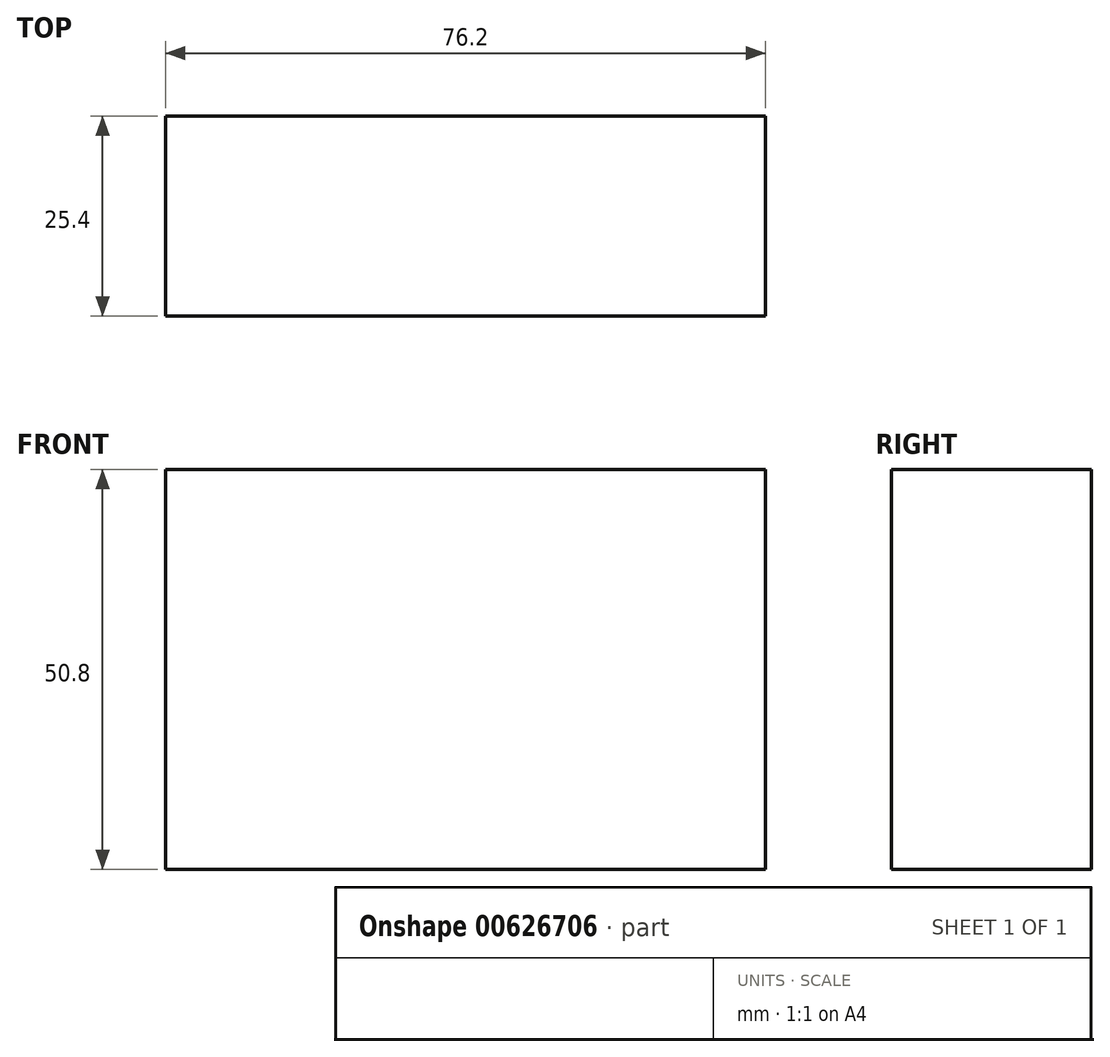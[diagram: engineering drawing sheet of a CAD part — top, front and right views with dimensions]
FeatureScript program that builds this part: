
annotation { "Feature Type Name" : "Feature", "Feature Type Description" : "" }
export const myFeature = defineFeature(function(context is Context, id is Id, definition is map)
    precondition{}
    {
        {
            var Q0;
            Q0=qCreatedBy(makeId("Front.planeOp"),FACE);
            var sketch = newSketch(context, id + "F0", { "sketchPlane" : qUnion([Q0])});
            skLineSegment(sketch, "E0.bottom", {"start": v(0, 0) * mm, "end": v(76.2, 0) * mm});
            skLineSegment(sketch, "E0.top", {"start": v(0, 50.8) * mm, "end": v(76.2, 50.8) * mm});
            skLineSegment(sketch, "E0.left", {"start": v(0, 0) * mm, "end": v(0, 50.8) * mm});
            skLineSegment(sketch, "E0.right", {"start": v(76.2, 0) * mm, "end": v(76.2, 50.8) * mm});
            skSolve(sketch);
        }
        {
            var Q0;
            Q0=makeQuery(id+"F0.imprint","IMPRINT",FACE,{"disambiguationData":[TD([[makeQuery(id+"F0.imprint","IMPRINT",EDGE,{"derivedFrom":sQuery(id+"F0.wireOp",EDGE,"E0.bottom")}),1.0]])]});
            extrude(context, id + "F1", {"entities" : qUnion([Q0]), "depth" : 25.4 * mm, "offsetDistance" : 25.4 * mm});
        }
    });
